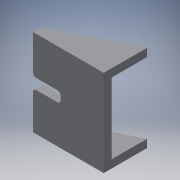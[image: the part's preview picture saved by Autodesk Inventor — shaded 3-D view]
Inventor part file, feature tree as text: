
AUTODESK INVENTOR PART (.ipt)
format: ipt  version: 2018 (Build 220112000, 112)  size: 142,336 bytes
history: native  units: mm
features: extrude x5, sketch x5, other x1, fillet x1
ambient origin geometry x8: Origin, YZ Plane, XZ Plane, XY Plane, X Axis, Y Axis, Z Axis, Center Point
bodies: Body1 (feature_tree)
feature tree (12):
  other  "ソリッド1"
  extrude  "押し出し1"  Depth=25.0mm
  extrude  "押し出し2"  Depth=25.0mm
  extrude  "押し出し3"  Depth=2.3mm
  extrude  "押し出し4"  Depth=25.0mm TaperAngle=0.0deg
  extrude  "押し出し5"  Depth=10.0mm TaperAngle=0.0deg
  fillet  "フィレット1"  Radius=10.0mm
  sketch  "スケッチ1"
  sketch  "スケッチ2"
  sketch  "スケッチ3"
  sketch  "スケッチ4"
  sketch  "スケッチ5"
